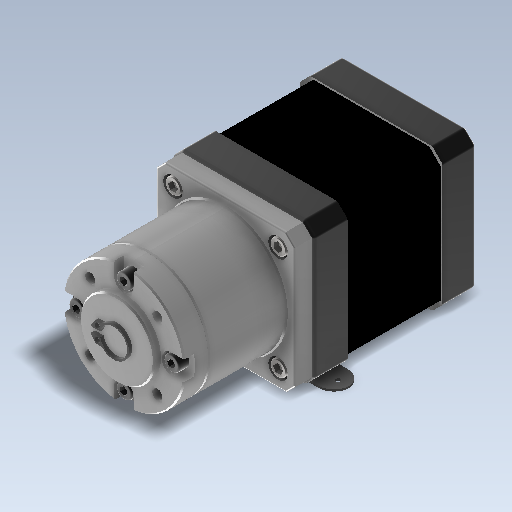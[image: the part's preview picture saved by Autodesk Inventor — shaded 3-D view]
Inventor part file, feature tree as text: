
AUTODESK INVENTOR PART (.ipt)
format: ipt  version: 2021 (Build 250183000, 183)  size: 1,530,880 bytes
history: native  units: mm
features: extrude x18, sketch x9, fillet x8, chamfer x5, pattern_linear x2, hole x2, plane x1, revolve x1, projected_geometry x1
ambient origin geometry x8: Origin, YZ Plane, XZ Plane, XY Plane, X Axis, Y Axis, Z Axis, Center Point
bodies: Solid1 (feature_tree)
feature tree (47):
  sketch  "Sketch1"  dims[d0=7.0mm d1=22.0mm]
  extrude  "Extrusion1"  Depth=22.0mm
  extrude  "Extrusion2"  Depth=31.0mm
  extrude  "Extrusion3"  Depth=3.0mm
  plane  "Work Plane2"
  extrude  "Extrusion7"  Depth=3.0mm
  extrude  "Extrusion8"  Depth=42.0mm
  chamfer  "Chamfer1"  Distance=27.577mm
  pattern_linear  "Rectangular Pattern2"  Spacing1=27.577mm  [1 undecoded]
  extrude  "Extrusion9"  Depth=24.0mm
  fillet  "Fillet1"  [1 undecoded]
  fillet  "Fillet2"  Radius=2.0mm
  chamfer  "Chamfer2"  [1 undecoded]
  fillet  "Fillet3"  Radius=48.0mm
  sketch  "Sketch11"  dims[d10=3.0mm d11=3.0mm]
  extrude  "Extrusion16"  TaperAngle=0.0deg  [1 undecoded]
  extrude  "Extrusion17"  [1 undecoded]
  extrude  "Extrusion18"  Depth=28.0mm
  extrude  "Extrusion19"  TaperAngle=0.0deg  [1 undecoded]
  extrude  "Extrusion20"  Depth=1.0mm
  extrude  "Extrusion21"  Depth=1.0mm
  extrude  "Extrusion22"  Depth=1.0mm
  extrude  "Extrusion23"  Depth=1.0mm
  extrude  "Extrusion24"  Depth=0.5mm
  extrude  "Extrusion25"  Depth=0.5mm
  fillet  "Fillet5"  Radius=0.5mm
  fillet  "Fillet6"  Radius=0.5mm
  fillet  "Fillet7"  Radius=0.5mm
  chamfer  "Chamfer3"  Distance=1.0mm
  chamfer  "Chamfer4"  Distance=1.0mm
  chamfer  "Chamfer5"  Distance=0.5mm
  extrude  "Extrusion28"  TaperAngle=0.0deg  [1 undecoded]
  revolve  "Revolution1"  Angle=45.0deg
  extrude  "Extrusion29"  Depth=560.0mm
  fillet  "Fillet8"  Radius=0.5mm
  hole  "Hole5"  [1 undecoded]
  pattern_linear  "Rectangular Pattern4"  Spacing1=0.0mm  [1 undecoded]
  fillet  "Fillet9"  Radius=47.0mm
  hole  "Hole6"  [1 undecoded]
  sketch  "Sketch4"  dims[d4=5.0mm d5=31.0mm]
  projected_geometry  "Projected Loop2"
  sketch  "Sketch5"  dims[d6=31.0mm d9=3.0mm]
  sketch  "Sketch12"  dims[d12=3.0mm d39=42.0mm]
  sketch  "Sketch13"  dims[d40=42.0mm]
  sketch  "Sketch14"  dims[d41=135.0deg]
  sketch  "Sketch15"  dims[d42=55.154mm]
  sketch  "Sketch16"  dims[d43=55.154mm d44=27.577mm d45=27.577mm d46=24.0mm d47=0.0mm d48=2.0mm d49=0.0mm d50=48.0mm d51=0.0mm d60=-10.0mm d126=28.0mm d127=0.0mm d128=1.0mm d129=1.0mm d130=1.0mm d131=1.0mm d132=0.5mm d134=0.5mm d135=0.5mm d136=0.5mm d137=0.5mm d138=1.0mm d139=1.0mm d140=0.5mm d141=0.0mm d145=0.125mm d146=2.0mm d147=45.0deg d148=560.0mm d150=0.5mm d187=48.0mm d188=0.0mm d189=47.0mm d190=0.0mm d191=1.0mm d192=1.0mm d193=0.5mm d194=2.0mm d195=45.0deg d196=0.5mm d239=41.0mm d240=41.0mm d241=36.0mm d242=22.0mm d243=40.0mm d245=360.0deg d247=5.0mm d248=0.0mm d249=30.0mm d250=0.0mm d251=6.0mm d252=0.0mm d253=3.0mm d254=0.0mm d255=3.0mm d256=0.0mm d257=1.8mm d258=0.0mm d259=5.0mm d260=0.0mm d261=5.0mm d262=0.0mm d263=1.5mm d264=0.0mm d265=2.0mm d266=0.0mm d271=0.5mm d272=0.3mm d273=0.5mm d274=0.4mm d275=2.0mm d276=45.0deg d277=0.4mm d278=2.0mm d279=45.0deg d280=0.4mm d281=2.0mm d282=45.0deg d283=1.0mm d284=0.0mm d285=22.0mm d286=0.5mm d287=135.0deg d288=90.0deg d292=8.0mm d293=5.0mm d294=5.0mm d295=0.0mm d296=0.0mm d300=4.5mm d301=1.4mm d302=6.0mm d303=4.0mm d304=2.0mm d305=90.0deg d306=8.0mm d307=0.0mm d308=20.0mm d310=44.0mm d311=4.5mm d312=1.4mm d313=6.0mm d314=4.0mm d315=2.0mm d316=90.0deg d317=8.0mm d318=0.0mm d319=4.25mm d320=4.25mm d267=0.5mm d268=0.872665mm]
note: 10 required parameter values undecoded (feature->parameter linkage not recoverable at this tier; creation-order binding heuristic only, values carry confidence <= 0.55)
